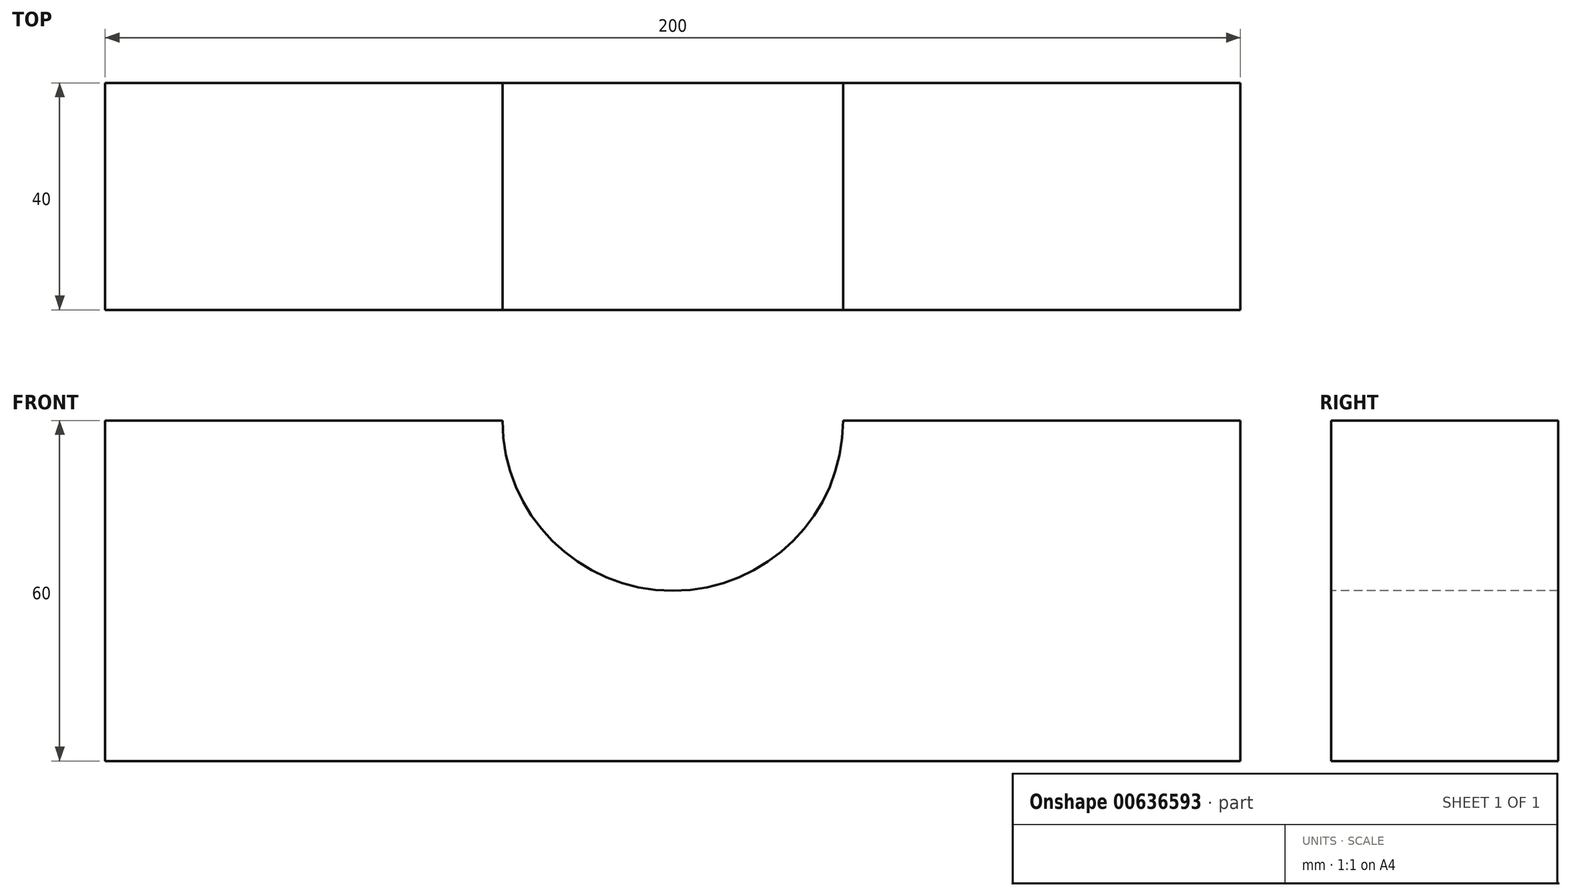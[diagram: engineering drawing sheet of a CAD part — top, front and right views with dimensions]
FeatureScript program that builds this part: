
annotation { "Feature Type Name" : "Feature", "Feature Type Description" : "" }
export const myFeature = defineFeature(function(context is Context, id is Id, definition is map)
    precondition{}
    {
        {
            var Q0;
            Q0=qCreatedBy(makeId("Right.planeOp"),FACE);
            var sketch = newSketch(context, id + "F0", { "sketchPlane" : qUnion([Q0])});
            skLineSegment(sketch, "E0.bottom", {"start": v(0, 0) * mm, "end": v(40, 0) * mm});
            skLineSegment(sketch, "E0.top", {"start": v(0, 60) * mm, "end": v(40, 60) * mm});
            skLineSegment(sketch, "E0.left", {"start": v(0, 0) * mm, "end": v(0, 60) * mm});
            skLineSegment(sketch, "E0.right", {"start": v(40, 0) * mm, "end": v(40, 60) * mm});
            skSolve(sketch);
        }
        {
            var Q0;
            Q0=makeQuery(id+"F0.imprint","IMPRINT",FACE,{"disambiguationData":[TD([[makeQuery(id+"F0.imprint","IMPRINT",EDGE,{"derivedFrom":sQuery(id+"F0.wireOp",EDGE,"E0.bottom")}),1.0]])]});
            extrude(context, id + "F1", {"entities" : qUnion([Q0]), "depth" : 200 * mm, "offsetDistance" : 25 * mm});
        }
        {
            var Q0;
            Q0=makeQuery(id+"F1.opExtrude","SWEPT_FACE",FACE,{"disambiguationData":[OSD([sQuery(id+"F0.wireOp",EDGE,"E0.left")])]});
            var sketch = newSketch(context, id + "F2", { "sketchPlane" : qUnion([Q0])});
            skPoint(sketch, "E1", {"position": v(100, 60) * mm});
            skSolve(sketch);
        }
        {
            var Q0;
            Q0=sQuery(id+"F2.wireOp",VERTEX,"E1");
            var Q1;
            Q1=makeQuery(id+"F1.opExtrude","SWEPT_BODY",BODY,{"disambiguationData":[OSD([sQuery(id+"F0.wireOp",EDGE,"E0.bottom"),sQuery(id+"F0.wireOp",EDGE,"E0.top"),sQuery(id+"F0.wireOp",EDGE,"E0.left"),sQuery(id+"F0.wireOp",EDGE,"E0.right")])]});
            hole(context, id + "F3", {"style" : HoleStyle.SIMPLE, "endStyle" : HoleEndStyle.THROUGH, "holeDiameter" : 60 * mm, "majorDiameter" : 5 * mm, "isTappedThrough" : true, "tappedDepth" : 12 * mm, "tapClearance" : 3, "locations" : qUnion([Q0]), "scope" : qUnion([Q1])});
        }
    });
